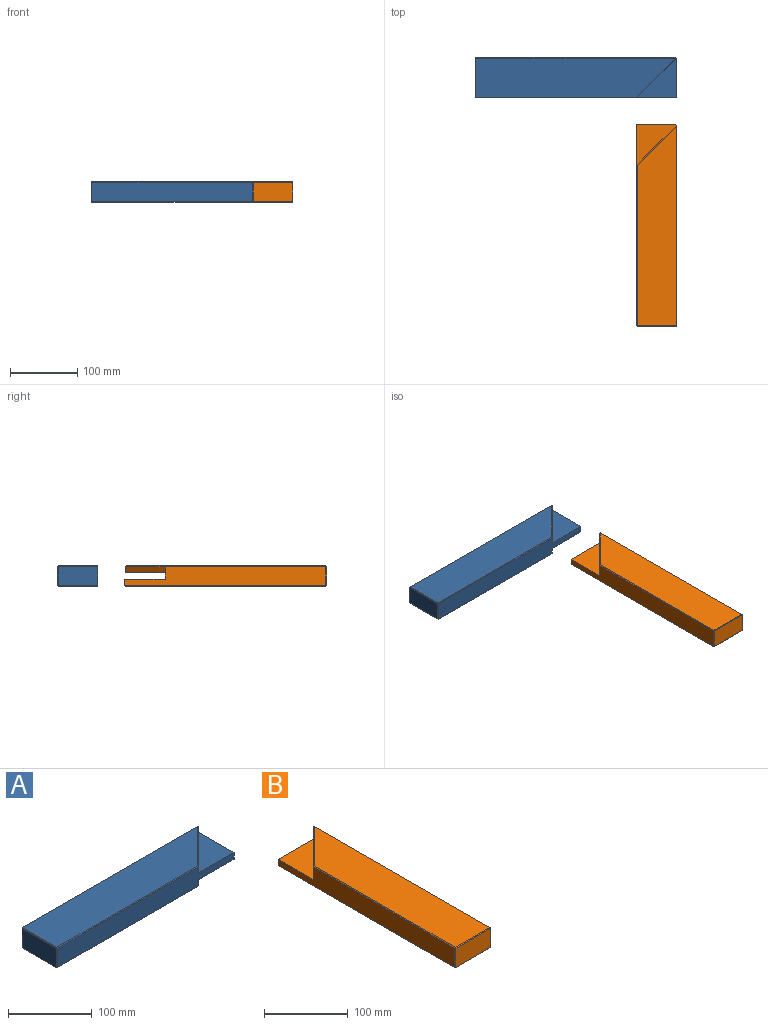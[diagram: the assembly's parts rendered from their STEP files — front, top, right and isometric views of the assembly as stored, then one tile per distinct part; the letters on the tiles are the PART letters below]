
ASSEMBLY  parts=2 mates=1
PART A: 24 faces, bbox 300x60x30 mm
  f0: plane 297x28mm, normal (0,1,0), area 7794mm2, adj f1,f9,f11,f15,f20,f23
  f1: plane 60x9mm, normal (1,0,0), area 540mm2, adj f0,f4,f9,f16
  f2: plane 58x10mm, normal (1,0,0), area 580mm2, adj f4,f8,f9,f23
  f3: plane 296.59x58mm, normal (0,0,1), area 15520mm2, adj f11,f12,f13,f14
  f4: plane 299x28mm, normal (0,-1,0), area 7292mm2, adj f1,f2,f7,f8,f9,f10,f14,f17
  f5: plane 240x58mm, normal (0,0,-1), area 13920mm2, adj f10,f15,f16,f21
  f6: plane 58x27.59mm, normal (-1,0,0), area 1599.8mm2, adj f17,f18,f19,f20,f21,f22
  f7: plane 59x59mm, normal (0.71,-0.71,0), area 750.9mm2, adj f4,f8,f13,f23
  f8: plane 60x59mm, normal (0,0,1), area 1799mm2, adj f2,f4,f7,f23
  f9: plane 60x60mm, normal (0,0,-1), area 3598mm2, adj f0,f1,f2,f4,f23
  f10: plane 240x1mm, normal (0,-0.71,-0.71), area 338.7mm2, adj f4,f5,f16,f19
  f11: plane 298.09x1mm, normal (0,0.71,0.71), area 420.7mm2, adj f0,f3,f12,f13,f20,f23
  f12: plane 59x0.71mm, normal (-0.71,0,0.71), area 58.6mm2, adj f3,f11,f14,f17,f18,f20
  f13: plane 59.41x59.41mm, normal (0.5,-0.5,0.71), area 117.4mm2, adj f3,f7,f11,f14,f23
  f14: plane 239.5x1mm, normal (0,-0.71,0.71), area 338.1mm2, adj f3,f4,f12,f13,f17
  f15: plane 240x1mm, normal (0,0.71,-0.71), area 338.7mm2, adj f0,f5,f16,f22
  f16: plane 60x1mm, normal (0.71,0,0.71), area 83.4mm2, adj f1,f5,f10,f15
  f17: plane 28.5x1mm, normal (-0.71,-0.71,0), area 39.6mm2, adj f4,f6,f12,f14,f18,f19
  f18: plane 58.59x0.71mm, normal (-0.92,0,0.38), area 44.6mm2, adj f6,f12,f17,f20
  f19: plane 1.41x1.41mm, normal (-0.71,-0.5,-0.5), area 1.4mm2, adj f6,f10,f17,f21
  f20: plane 28.5x1mm, normal (-0.71,0.71,0), area 39.6mm2, adj f0,f6,f11,f12,f18,f22
  f21: plane 58x1mm, normal (-0.71,0,-0.71), area 81.4mm2, adj f5,f6,f19,f22
  f22: plane 1.41x1.41mm, normal (-0.71,0.5,-0.5), area 1.4mm2, adj f6,f15,f20,f21
  f23: plane 19.59x2mm, normal (0.71,0.71,0), area 41.4mm2, adj f0,f2,f7,f8,f9,f11,f13
PART B: 26 faces, bbox 60x300x30 mm
  f0: plane 58x9mm, normal (0,1,0), area 522mm2, adj f4,f9,f14,f24
  f1: plane 297x28mm, normal (1,0,0), area 7736mm2, adj f6,f8,f9,f10,f13,f17,f24,f25
  f2: plane 296.59x58mm, normal (0,0,1), area 15520mm2, adj f10,f11,f12,f21
  f3: plane 298x58mm, normal (0,0,-1), area 17284mm2, adj f13,f14,f15,f18
  f4: plane 299x28mm, normal (-1,0,0), area 7232mm2, adj f0,f6,f7,f9,f11,f15,f22
  f5: plane 58x28mm, normal (0,-1,0), area 1623.7mm2, adj f16,f17,f18,f19,f20,f21,f22,f23
  f6: plane 60x10mm, normal (0,1,0), area 600mm2, adj f1,f4,f8,f9
  f7: plane 59x59mm, normal (-0.71,0.71,0), area 750.9mm2, adj f4,f8,f12,f25
  f8: plane 60x59mm, normal (0,0,-1), area 1799mm2, adj f1,f6,f7,f25
  f9: plane 60x60mm, normal (0,0,1), area 3598mm2, adj f0,f1,f4,f6,f24
  f10: plane 297.59x1mm, normal (0.71,0,0.71), area 420.3mm2, adj f1,f2,f12,f19,f25
  f11: plane 239x1mm, normal (-0.71,0,0.71), area 337.7mm2, adj f2,f4,f12,f23
  f12: plane 59.41x59.41mm, normal (-0.5,0.5,0.71), area 117.4mm2, adj f2,f7,f10,f11,f25
  f13: plane 298x1mm, normal (0.71,0,-0.71), area 420.7mm2, adj f1,f3,f16,f24
  f14: plane 59x1mm, normal (0,0.71,-0.71), area 82mm2, adj f0,f3,f15,f24
  f15: plane 299x1mm, normal (-0.71,0,-0.71), area 422.1mm2, adj f3,f4,f14,f20
  f16: plane 1.41x1.41mm, normal (0.5,-0.71,-0.5), area 1.4mm2, adj f5,f13,f17,f18
  f17: plane 28x1mm, normal (0.71,-0.71,0), area 39mm2, adj f1,f5,f16,f19
  f18: plane 58x1mm, normal (0,-0.71,-0.71), area 81.4mm2, adj f3,f5,f16,f20
  f19: plane 1.41x1.41mm, normal (0.5,-0.71,0.5), area 1.4mm2, adj f5,f10,f17,f21
  f20: plane 1.41x1.41mm, normal (-0.5,-0.71,-0.5), area 1.4mm2, adj f5,f15,f18,f22
  f21: plane 58x1mm, normal (0,-0.71,0.71), area 81.4mm2, adj f2,f5,f19,f23
  f22: plane 28x1mm, normal (-0.71,-0.71,0), area 39mm2, adj f4,f5,f20,f23
  f23: plane 1.41x1.41mm, normal (-0.5,-0.71,0.5), area 1.4mm2, adj f5,f11,f21,f22
  f24: plane 10x2mm, normal (0.71,0.71,0), area 26.9mm2, adj f0,f1,f9,f13,f14
  f25: plane 9.59x1mm, normal (0.71,0.71,0), area 13.1mm2, adj f1,f7,f8,f10,f12
PLACE A t=(-141.13,180.86,-11.43)mm
PLACE B t=(-141.13,80.83,-11.43)mm fixed
MATE slider A.f4 <-> B.f6  axis (0,-1,0) through (-141.13,180.86,3.57)mm
